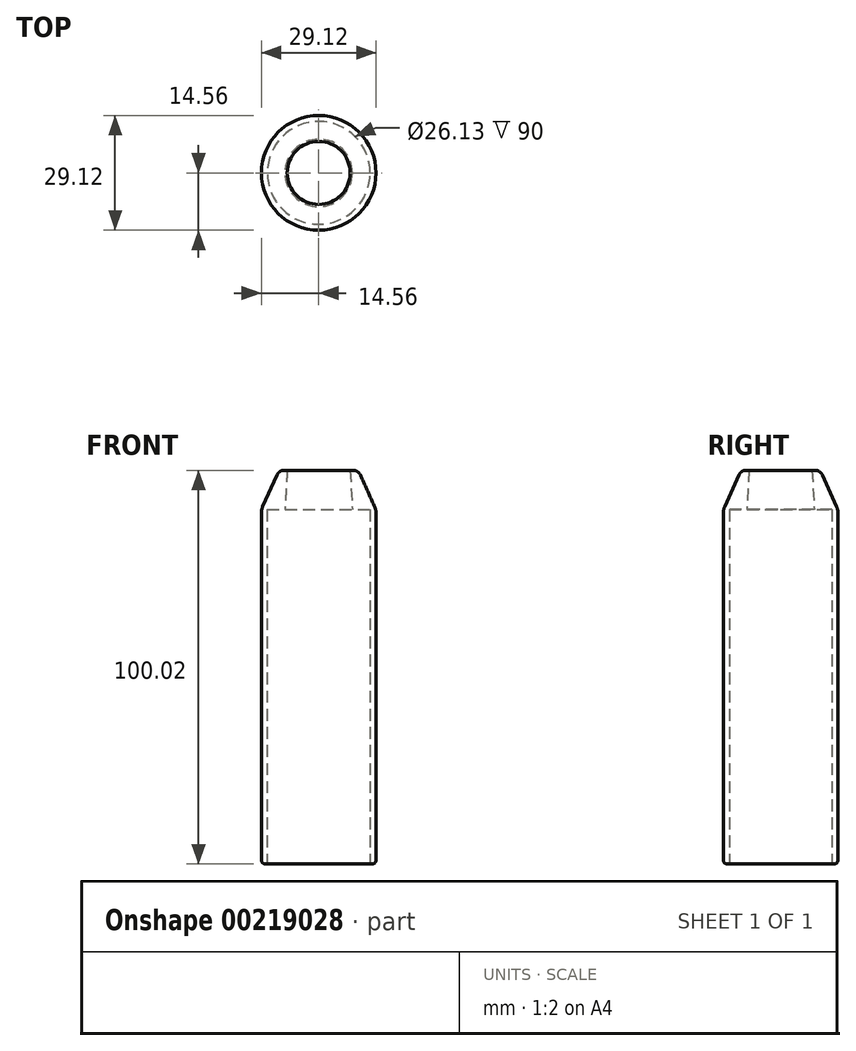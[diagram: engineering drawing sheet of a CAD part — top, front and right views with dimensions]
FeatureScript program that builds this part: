
annotation { "Feature Type Name" : "Feature", "Feature Type Description" : "" }
export const myFeature = defineFeature(function(context is Context, id is Id, definition is map)
    precondition{}
    {
        {
            var Q0;
            Q0=qCreatedBy(makeId("Front.planeOp"),FACE);
            var sketch = newSketch(context, id + "F0", { "sketchPlane" : qUnion([Q0])});
            skLineSegment(sketch, "E0", {"start": v(8, 95.02) * mm, "end": v(8.56, 85.04) * mm});
            skLineSegment(sketch, "E1", {"start": v(8.56, 85.04) * mm, "end": v(13.06, 85.04) * mm});
            skLineSegment(sketch, "E2", {"start": v(13.06, 85.04) * mm, "end": v(13.06, -4.96) * mm});
            skLineSegment(sketch, "E3", {"start": v(8, 95.02) * mm, "end": v(10, 95.14) * mm});
            skLineSegment(sketch, "E4", {"start": v(10, 95.14) * mm, "end": v(14.56, 85.04) * mm});
            skLineSegment(sketch, "E5", {"start": v(14.56, 85.04) * mm, "end": v(14.56, -4.96) * mm});
            skLineSegment(sketch, "E6", {"start": v(13.06, -4.96) * mm, "end": v(14.56, -4.96) * mm});
            skSolve(sketch);
        }
        {
            var Q0;
            Q0=qCreatedBy(makeId("Front.planeOp"),FACE);
            var sketch = newSketch(context, id + "F1", { "sketchPlane" : qUnion([Q0])});
            skLineSegment(sketch, "E7", {"start": v(0, 0) * mm, "end": v(0, 96) * mm, "construction": true});
            skSolve(sketch);
        }
        {
            var Q0;
            Q0=makeQuery(id+"F0.imprint","IMPRINT",FACE,{"disambiguationData":[TD([[makeQuery(id+"F0.imprint","IMPRINT",EDGE,{"derivedFrom":sQuery(id+"F0.wireOp",EDGE,"E0")}),1.0]])]});
            var Q1;
            Q1=sQuery(id+"F1.wireOp",EDGE,"E7");
            revolve(context, id + "F2", {"entities" : qUnion([Q0]), "axis" : qUnion([Q1]), "revolveType" : RevolveType.FULL});
        }
        {
            var Q0;
            Q0=makeQuery(id+"F2.opRevolve","SWEPT_EDGE",EDGE,{"disambiguationData":[OSD([sQuery(id+"F0.wireOp",EDGE,"E3"),sQuery(id+"F0.wireOp",EDGE,"E4")])]});
            fillet(context, id + "F3", {"entities" : qUnion([Q0]), "radius" : 2 * mm, "tangentPropagation" : true, "allowEdgeOverflow" : false});
        }
        {
            var Q0;
            Q0=makeQuery(id+"F2.opRevolve","SWEPT_EDGE",EDGE,{"disambiguationData":[OSD([sQuery(id+"F0.wireOp",EDGE,"E4"),sQuery(id+"F0.wireOp",EDGE,"E5")])]});
            fillet(context, id + "F4", {"entities" : qUnion([Q0]), "radius" : 4 * mm, "tangentPropagation" : true, "allowEdgeOverflow" : false});
        }
        {
            var Q0;
            Q0=makeQuery(id+"F2.opRevolve","SWEPT_EDGE",EDGE,{"disambiguationData":[OSD([sQuery(id+"F0.wireOp",EDGE,"E5"),sQuery(id+"F0.wireOp",EDGE,"E6")])]});
            fillet(context, id + "F5", {"entities" : qUnion([Q0]), "radius" : 1 * mm, "tangentPropagation" : true, "allowEdgeOverflow" : false});
        }
    });
